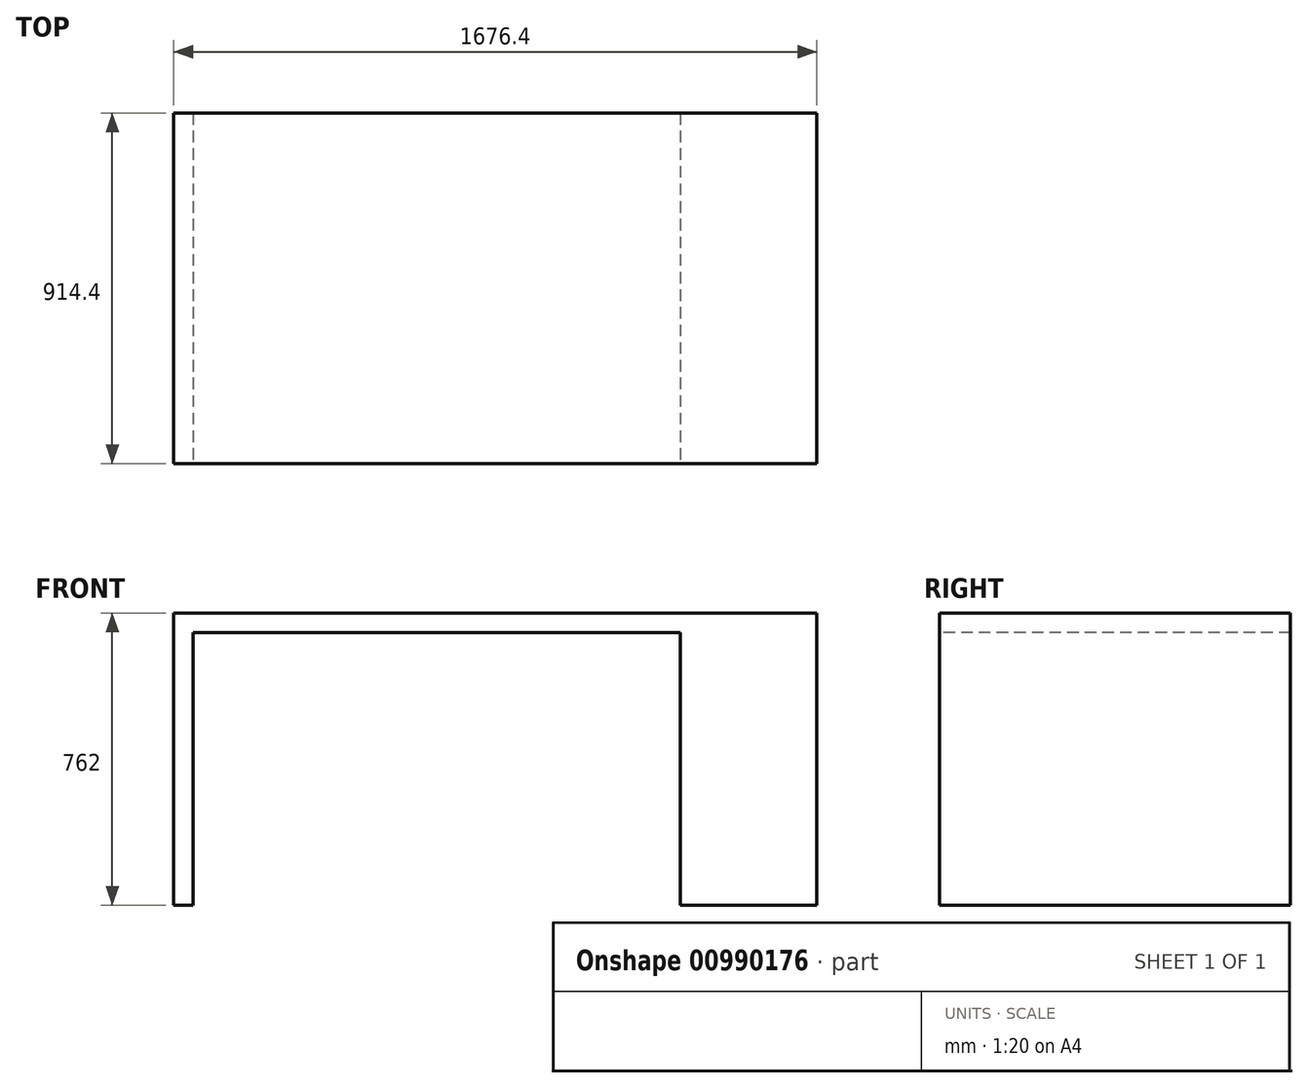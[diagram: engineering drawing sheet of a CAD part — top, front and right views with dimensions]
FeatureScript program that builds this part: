
annotation { "Feature Type Name" : "Feature", "Feature Type Description" : "" }
export const myFeature = defineFeature(function(context is Context, id is Id, definition is map)
    precondition{}
    {
        {
            var Q0;
            Q0=qCreatedBy(makeId("Top.planeOp"),FACE);
            var sketch = newSketch(context, id + "F0", { "sketchPlane" : qUnion([Q0])});
            skLineSegment(sketch, "E0.bottom", {"start": v(838.2, -457.2) * mm, "end": v(-838.2, -457.2) * mm});
            skLineSegment(sketch, "E0.top", {"start": v(838.2, 457.2) * mm, "end": v(-838.2, 457.2) * mm});
            skLineSegment(sketch, "E0.left", {"start": v(838.2, -457.2) * mm, "end": v(838.2, 457.2) * mm});
            skLineSegment(sketch, "E0.right", {"start": v(-838.2, -457.2) * mm, "end": v(-838.2, 457.2) * mm});
            skPoint(sketch, "E0.middle", {"position": v(0, 0) * mm});
            skSolve(sketch);
        }
        {
            var Q0;
            Q0 = qSketchRegion(id + "F0", true);
            extrude(context, id + "F1", {"entities" : qUnion([Q0]), "depth" : 762 * mm, "offsetDistance" : 25.4 * mm});
        }
        {
            var Q0;
            Q0=makeQuery(id+"F1.opExtrude","SWEPT_FACE",FACE,{"disambiguationData":[OSD([sQuery(id+"F0.wireOp",EDGE,"E0.bottom")])]});
            var sketch = newSketch(context, id + "F2", { "sketchPlane" : qUnion([Q0])});
            skLineSegment(sketch, "E1.bottom", {"start": v(-787.4, 711.2) * mm, "end": v(482.6, 711.2) * mm});
            skLineSegment(sketch, "E1.top", {"start": v(-787.4, 0) * mm, "end": v(482.6, 0) * mm});
            skLineSegment(sketch, "E1.left", {"start": v(-787.4, 711.2) * mm, "end": v(-787.4, 0) * mm});
            skLineSegment(sketch, "E1.right", {"start": v(482.6, 711.2) * mm, "end": v(482.6, 0) * mm});
            skSolve(sketch);
        }
        {
            var Q0;
            Q0 = qSketchRegion(id + "F2", true);
            extrude(context, id + "F3", {"entities" : qUnion([Q0]), "operationType" : NewBodyOperationType.REMOVE, "endBound" : BoundingType.UP_TO_NEXT, "oppositeDirection" : true, "depth" : 25.4 * mm, "offsetDistance" : 25.4 * mm});
        }
    });
